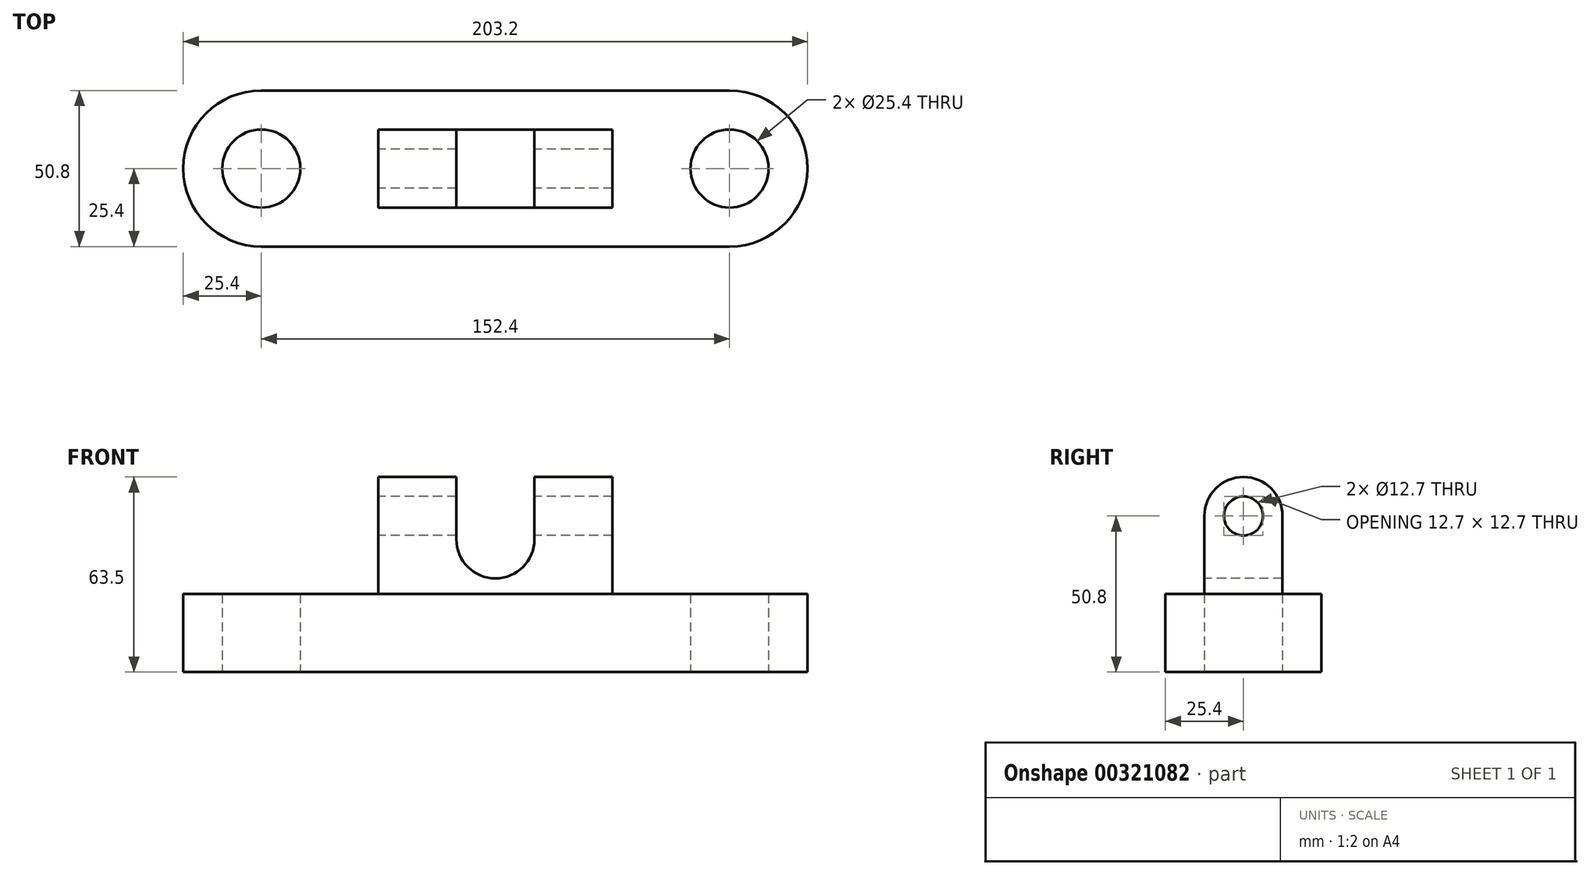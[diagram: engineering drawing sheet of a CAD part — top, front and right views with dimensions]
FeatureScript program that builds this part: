
annotation { "Feature Type Name" : "Feature", "Feature Type Description" : "" }
export const myFeature = defineFeature(function(context is Context, id is Id, definition is map)
    precondition{}
    {
        {
            var Q0;
            Q0=qCreatedBy(makeId("Top.planeOp"),FACE);
            var sketch = newSketch(context, id + "F0", { "sketchPlane" : qUnion([Q0])});
            skLineSegment(sketch, "E0.bottom", {"start": v(-76.2, 25.4) * mm, "end": v(76.2, 25.4) * mm});
            skLineSegment(sketch, "E0.top", {"start": v(-76.2, -25.4) * mm, "end": v(76.2, -25.4) * mm});
            skArc(sketch, "E1", {"start": v(-76.2, 25.4) * mm, "mid": v(-101.6, 0) * mm, "end": v(-76.2, -25.4) * mm});
            skArc(sketch, "E2", {"start": v(76.2, -25.4) * mm, "mid": v(101.6, 0) * mm, "end": v(76.2, 25.4) * mm});
            skCircle(sketch, "E3", {"center": v(76.2, 0) * mm, "radius": 12.7 * mm});
            skCircle(sketch, "E4", {"center": v(-76.2, 0) * mm, "radius": 12.7 * mm});
            skSolve(sketch);
        }
        {
            var Q0;
            Q0 = qSketchRegion(id + "F0", true);
            extrude(context, id + "F1", {"entities" : qUnion([Q0]), "depth" : 25.4 * mm});
        }
        {
            var Q0;
            Q0=qCreatedBy(makeId("Right.planeOp"),FACE);
            var sketch = newSketch(context, id + "F2", { "sketchPlane" : qUnion([Q0])});
            skLineSegment(sketch, "E5.top", {"start": v(-12.7, 25.4) * mm, "end": v(12.7, 25.4) * mm});
            skLineSegment(sketch, "E5.left", {"start": v(-12.7, 50.8) * mm, "end": v(-12.7, 25.4) * mm});
            skLineSegment(sketch, "E5.right", {"start": v(12.7, 50.8) * mm, "end": v(12.7, 25.4) * mm});
            skArc(sketch, "E6", {"start": v(12.7, 50.8) * mm, "mid": v(0, 63.5) * mm, "end": v(-12.7, 50.8) * mm});
            skCircle(sketch, "E7", {"center": v(0, 50.8) * mm, "radius": 6.35 * mm});
            skSolve(sketch);
        }
        {
            var Q0;
            Q0 = qSketchRegion(id + "F2", true);
            extrude(context, id + "F3", {"entities" : qUnion([Q0]), "operationType" : NewBodyOperationType.ADD, "depth" : 38.1 * mm, "hasSecondDirection" : true, "secondDirectionOppositeDirection" : true, "secondDirectionDepth" : 38.1 * mm});
        }
        {
            var Q0;
            Q0=qCreatedBy(makeId("Front.planeOp"),FACE);
            var sketch = newSketch(context, id + "F4", { "sketchPlane" : qUnion([Q0])});
            skLineSegment(sketch, "E8.bottom", {"start": v(12.7, 63.5) * mm, "end": v(-12.7, 63.5) * mm});
            skLineSegment(sketch, "E8.left", {"start": v(12.7, 63.5) * mm, "end": v(12.7, 43.18) * mm});
            skLineSegment(sketch, "E8.right", {"start": v(-12.7, 63.5) * mm, "end": v(-12.7, 43.18) * mm});
            skArc(sketch, "E9", {"start": v(-12.7, 43.18) * mm, "mid": v(0, 30.48) * mm, "end": v(12.7, 43.18) * mm});
            skSolve(sketch);
        }
        {
            var Q0;
            Q0 = qSketchRegion(id + "F4", true);
            extrude(context, id + "F5", {"entities" : qUnion([Q0]), "operationType" : NewBodyOperationType.REMOVE, "oppositeDirection" : true, "depth" : 25.4 * mm, "hasSecondDirection" : true, "secondDirectionOppositeDirection" : false, "secondDirectionDepth" : 25.4 * mm});
        }
    });
